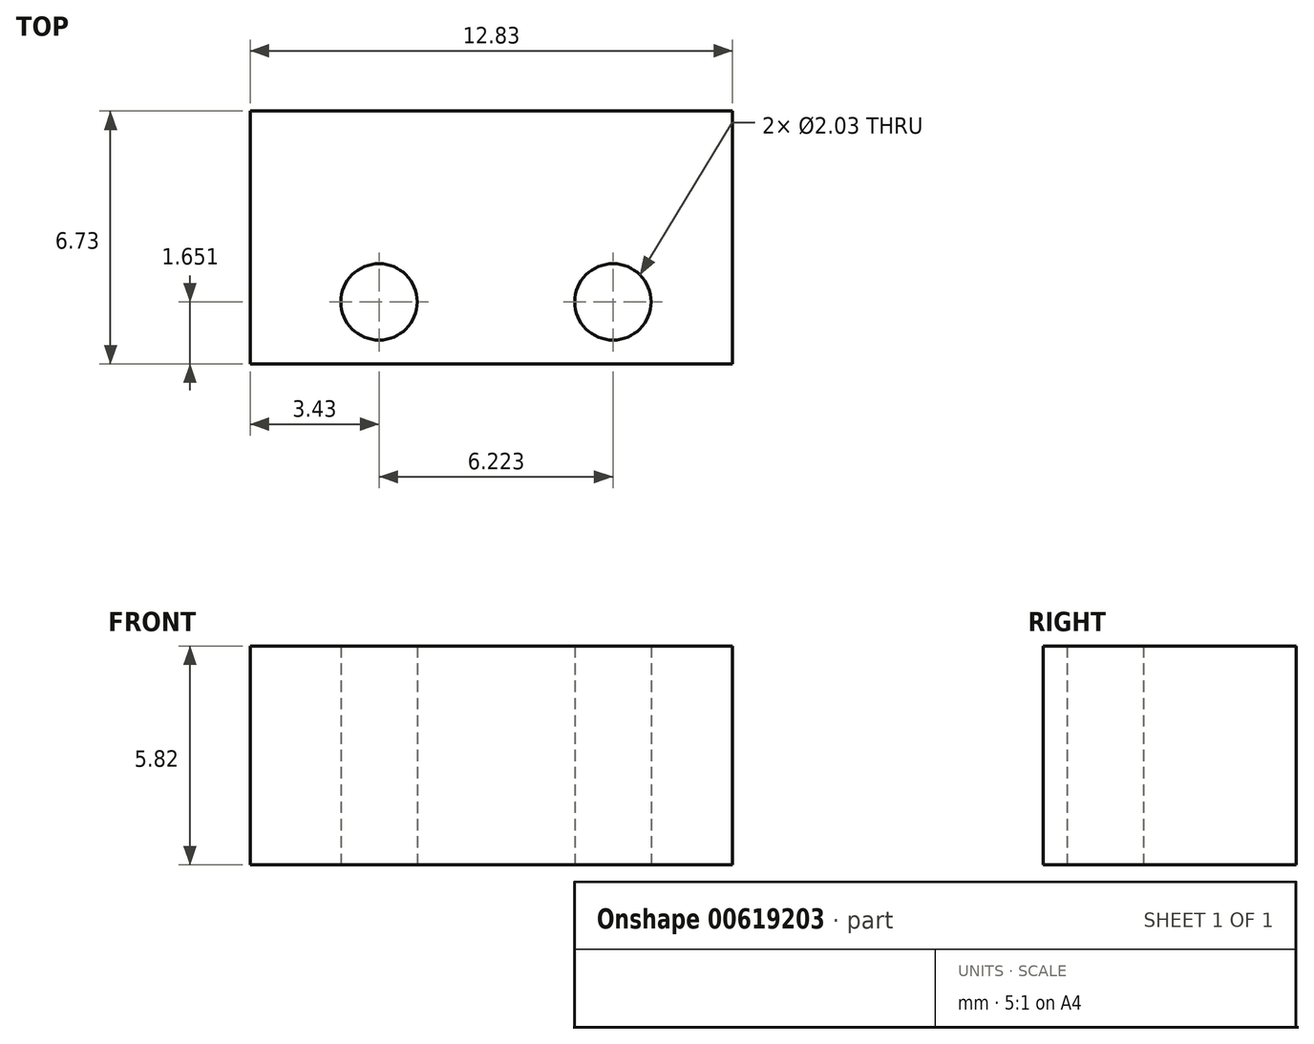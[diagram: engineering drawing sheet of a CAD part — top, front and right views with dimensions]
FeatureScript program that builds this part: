
annotation { "Feature Type Name" : "Feature", "Feature Type Description" : "" }
export const myFeature = defineFeature(function(context is Context, id is Id, definition is map)
    precondition{}
    {
        {
            var Q0;
            Q0=qCreatedBy(makeId("Top.planeOp"),FACE);
            var sketch = newSketch(context, id + "F0", { "sketchPlane" : qUnion([Q0])});
            skLineSegment(sketch, "E0.bottom", {"start": v(-5.5, 2.15) * mm, "end": v(7.33, 2.15) * mm});
            skLineSegment(sketch, "E0.top", {"start": v(-5.5, -4.58) * mm, "end": v(7.33, -4.58) * mm});
            skLineSegment(sketch, "E0.left", {"start": v(-5.5, 2.15) * mm, "end": v(-5.5, -4.58) * mm});
            skLineSegment(sketch, "E0.right", {"start": v(7.33, 2.15) * mm, "end": v(7.33, -4.58) * mm});
            skCircle(sketch, "E1", {"center": v(-2.07, -2.93) * mm, "radius": 1.02 * mm});
            skCircle(sketch, "E2", {"center": v(4.15, -2.93) * mm, "radius": 1.02 * mm});
            skSolve(sketch);
        }
        {
            var Q0;
            Q0=qSketchRegion(id+"F0",true);
            extrude(context, id + "F1", {"entities" : qUnion([Q0]), "depth" : 5.82 * mm});
        }
    });
